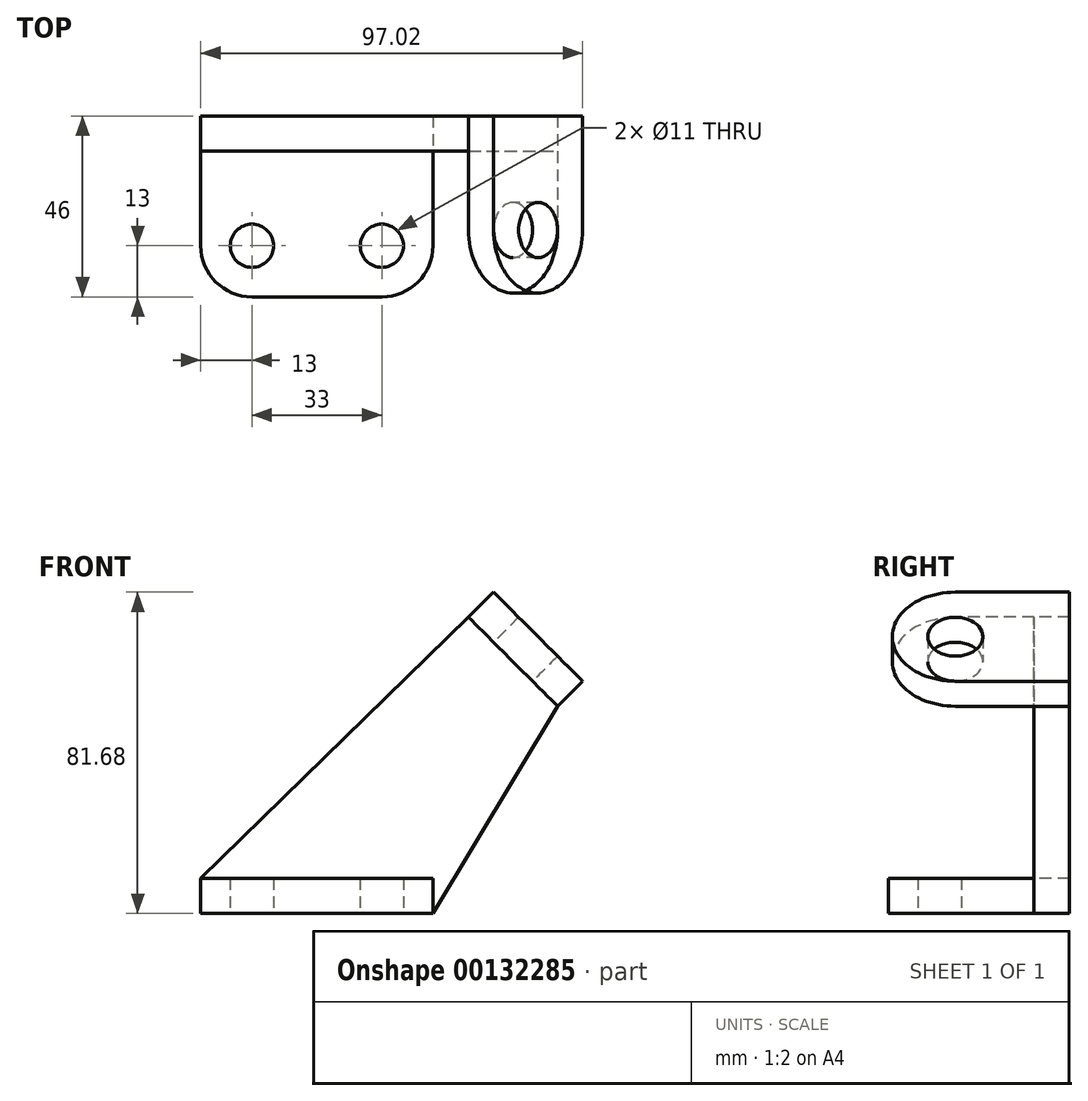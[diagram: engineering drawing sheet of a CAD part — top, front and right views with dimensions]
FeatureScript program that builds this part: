
annotation { "Feature Type Name" : "Feature", "Feature Type Description" : "" }
export const myFeature = defineFeature(function(context is Context, id is Id, definition is map)
    precondition{}
    {
        {
            var Q0;
            Q0=qCreatedBy(makeId("Top.planeOp"),FACE);
            var sketch = newSketch(context, id + "F0", { "sketchPlane" : qUnion([Q0])});
            skLineSegment(sketch, "E0", {"start": v(0, 0) * mm, "end": v(59, 0) * mm});
            skLineSegment(sketch, "E1", {"start": v(59, 0) * mm, "end": v(59, -24) * mm});
            skLineSegment(sketch, "E2", {"start": v(0, 0) * mm, "end": v(0, -24) * mm});
            skArc(sketch, "E3", {"start": v(0, -24) * mm, "mid": v(3.8, -33.2) * mm, "end": v(13, -37) * mm});
            skArc(sketch, "E4", {"start": v(46, -37) * mm, "mid": v(55.2, -33.2) * mm, "end": v(59, -24) * mm});
            skLineSegment(sketch, "E5", {"start": v(13, -37) * mm, "end": v(46, -37) * mm});
            skCircle(sketch, "E6", {"center": v(13, -24) * mm, "radius": 5.5 * mm});
            skCircle(sketch, "E7", {"center": v(46, -24) * mm, "radius": 5.5 * mm});
            skSolve(sketch);
        }
        {
            var Q0;
            Q0=makeQuery(id+"F0.imprint","IMPRINT",FACE,{"disambiguationData":[TD([[makeQuery(id+"F0.imprint","IMPRINT",EDGE,{"derivedFrom":sQuery(id+"F0.wireOp",EDGE,"E0")}),-1.0]])]});
            extrude(context, id + "F1", {"entities" : qUnion([Q0]), "depth" : 9 * mm});
        }
        {
            var Q0;
            Q0=makeQuery(id+"F1.opExtrude","SWEPT_FACE",FACE,{"disambiguationData":[OSD([sQuery(id+"F0.wireOp",EDGE,"E0")])]});
            var sketch = newSketch(context, id + "F2", { "sketchPlane" : qUnion([Q0])});
            skLineSegment(sketch, "E8", {"start": v(-59, 0) * mm, "end": v(-90.65, 52.69) * mm});
            skLineSegment(sketch, "E9", {"start": v(0, 9) * mm, "end": v(-68.03, 75.31) * mm});
            skLineSegment(sketch, "E10", {"start": v(-68.03, 75.31) * mm, "end": v(-90.65, 52.69) * mm});
            skLineSegment(sketch, "E11", {"start": v(-79.34, 64) * mm, "end": v(-109.43, 64) * mm, "construction": true});
            skSolve(sketch);
        }
        {
            var Q0;
            Q0=makeQuery(id+"F2.imprint","IMPRINT",FACE,{"disambiguationData":[TD([[makeQuery(id+"F2.imprint","IMPRINT",EDGE,{"derivedFrom":sQuery(id+"F2.wireOp",EDGE,"E8")}),-1.0]])]});
            var Q1;
            {var subQ0=sQuery(id+"F0.wireOp",EDGE,"E0");Q1=makeQuery(id+"F2.imprint","IMPRINT",FACE,{"disambiguationData":[TD([[makeQuery(id+"F2.imprint","IMPRINT",EDGE,{"derivedFrom":makeQuery(id+"F1.opExtrude","CAP_EDGE",EDGE,{"disambiguationData":[OSD([subQ0])],"isStart":true})}),-1.0]])]});}
            extrude(context, id + "F3", {"entities" : qUnion([Q0, Q1]), "operationType" : NewBodyOperationType.ADD, "depth" : 9 * mm});
        }
        {
            var Q0;
            Q0=makeQuery(id+"F3.opExtrude","SWEPT_FACE",FACE,{"disambiguationData":[OSD([sQuery(id+"F2.wireOp",EDGE,"E10")])]});
            var sketch = newSketch(context, id + "F4", { "sketchPlane" : qUnion([Q0])});
            skLineSegment(sketch, "E12", {"start": v(9, 5.15) * mm, "end": v(-20, 5.15) * mm});
            skLineSegment(sketch, "E13", {"start": v(9, -26.85) * mm, "end": v(-20, -26.85) * mm});
            skPoint(sketch, "E13.endSnap0", {"position": v(4.5, -26.85) * mm});
            skArc(sketch, "E14", {"start": v(-20, 5.15) * mm, "mid": v(-36, -10.85) * mm, "end": v(-20, -26.85) * mm});
            skCircle(sketch, "E15", {"center": v(-20, -10.85) * mm, "radius": 7 * mm});
            skLineSegment(sketch, "E16", {"start": v(9, -10.85) * mm, "end": v(-36, -10.85) * mm, "construction": true});
            skLineSegment(sketch, "E17", {"start": v(-20, 5.15) * mm, "end": v(-20, -26.85) * mm, "construction": true});
            skLineSegment(sketch, "E18", {"start": v(9, 5.15) * mm, "end": v(9, -26.85) * mm});
            skSolve(sketch);
        }
        {
            var Q0;
            {var subQ0=sQuery(id+"F4.wireOp",EDGE,"E14");Q0=makeQuery(id+"F4.imprint","IMPRINT",FACE,{"disambiguationData":[TD([[makeQuery(id+"F4.imprint","IMPRINT",EDGE,{"derivedFrom":subQ0}),1.0]])]});}
            var Q1;
            {var subQ2=sQuery(id+"F4.wireOp",EDGE,"E18");Q1=makeQuery(id+"F4.imprint","IMPRINT",FACE,{"disambiguationData":[TD([[makeQuery(id+"F4.imprint","IMPRINT",EDGE,{"derivedFrom":subQ2}),-1.0]])]});}
            extrude(context, id + "F5", {"entities" : qUnion([Q0, Q1]), "operationType" : NewBodyOperationType.ADD, "depth" : 9 * mm});
        }
    });
